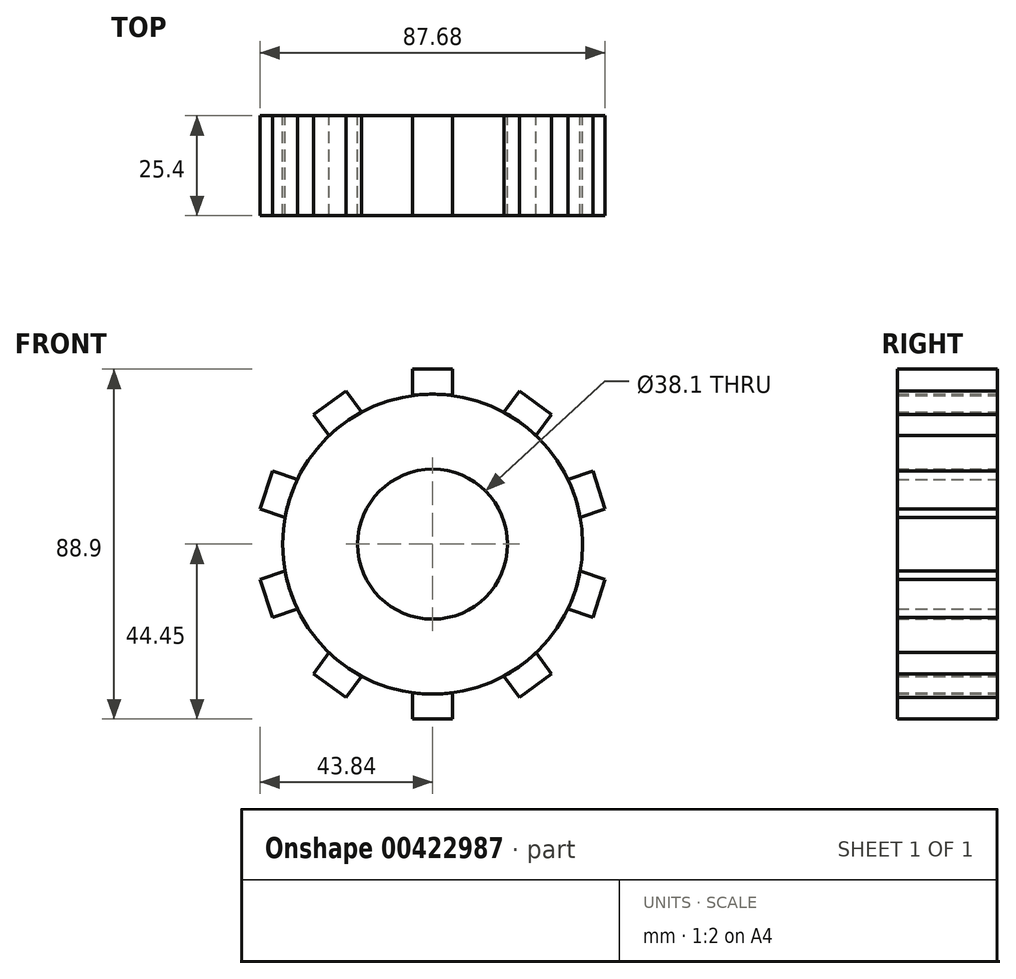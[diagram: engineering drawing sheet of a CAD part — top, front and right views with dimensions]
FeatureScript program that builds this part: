
annotation { "Feature Type Name" : "Feature", "Feature Type Description" : "" }
export const myFeature = defineFeature(function(context is Context, id is Id, definition is map)
    precondition{}
    {
        {
            var Q0;
            Q0=qCreatedBy(makeId("Front.planeOp"),FACE);
            var sketch = newSketch(context, id + "F0", { "sketchPlane" : qUnion([Q0])});
            skCircle(sketch, "E0", {"center": v(0, 0) * mm, "radius": 38.1 * mm});
            skCircle(sketch, "E1", {"center": v(0, 0) * mm, "radius": 19.05 * mm});
            skSolve(sketch);
        }
        {
            var Q0;
            Q0 = qSketchRegion(id + "F0", true);
            extrude(context, id + "F1", {"entities" : qUnion([Q0]), "endBound" : BoundingType.SYMMETRIC, "depth" : 25.4 * mm});
        }
        {
            var Q0;
            Q0=qCreatedBy(makeId("Front.planeOp"),FACE);
            var sketch = newSketch(context, id + "F2", { "sketchPlane" : qUnion([Q0])});
            skArc(sketch, "E2.0", {"start": v(5.08, 37.76) * mm, "mid": v(0, 38.1) * mm, "end": v(-5.08, 37.76) * mm});
            skLineSegment(sketch, "E3.top", {"start": v(-5.08, 44.45) * mm, "end": v(5.08, 44.45) * mm});
            skLineSegment(sketch, "E3.left", {"start": v(-5.08, 37.76) * mm, "end": v(-5.08, 44.45) * mm});
            skLineSegment(sketch, "E3.right", {"start": v(5.08, 37.76) * mm, "end": v(5.08, 44.45) * mm});
            skSolve(sketch);
        }
        {
            var Q0;
            Q0 = qSketchRegion(id + "F2", true);
            extrude(context, id + "F3", {"entities" : qUnion([Q0]), "endBound" : BoundingType.SYMMETRIC, "depth" : 25.4 * mm});
        }
        {
            var Q0;
            Q0=makeQuery(id+"F3.opExtrude","SWEPT_BODY",BODY,{"disambiguationData":[OSD([sQuery(id+"F2.wireOp",EDGE,"E2.0"),sQuery(id+"F2.wireOp",EDGE,"E3.top"),sQuery(id+"F2.wireOp",EDGE,"E3.left"),sQuery(id+"F2.wireOp",EDGE,"E3.right")])]});
            var Q1;
            Q1=makeQuery(id+"F1.opExtrude","SWEPT_FACE",FACE,{"disambiguationData":[OSD([sQuery(id+"F0.wireOp",EDGE,"E1")])]});
            circularPattern(context, id + "F4", {"entities" : qUnion([Q0]), "axis" : qUnion([Q1]), "angle" : 360 * degree, "instanceCount" : 10, "equalSpace" : true});
        }
    });
